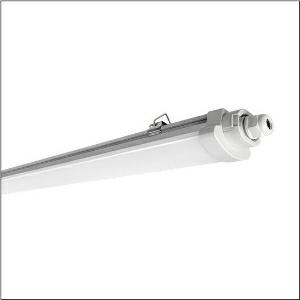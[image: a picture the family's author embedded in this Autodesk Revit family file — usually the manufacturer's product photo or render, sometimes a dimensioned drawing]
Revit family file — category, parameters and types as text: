
# Revit family: monsun_r__41_51fk20mn460a_a5b0
name_source: partatom
category: Lighting Fixtures
units: mm (PartAtom-declared; Revit-internal decimal feet)

## family parameters
Cut with Voids When Loaded = No
Host = Face
Light Source = No
Part Type = Normal
Room Calculation Point = No
Round Connector Dimension = Use Diameter
Shared = No

## types (1)
- --- (1 x LED, 6000 lm, 46 W, 4000K)
    Apparent Load = 46 VA
    CIE Flux Codes = 44 74 91 91 100
    Color Rendering = 80
    Color Temperature = 4000K
    Default Elevation = 1800 mm
    Description = Monsun® 41, damp-proof luminaire, primary optical cover: diffuser, of PC, frosted, light emission: direct distribution, primary light characteristic: symmetric, installation type: suspended mounting, surface-mounted, LED, rated luminous flux: 6.000lm, luminous efficacy: 130lm/W, light colour: 840, colour temperature: 4000K, control gear: ON/OFF Multilumen, with terminal, 3-pole, mains connection: 220..240V, AC, 50/60Hz, rated input power: 46W, housing, luminaire housing, of PC, grey, length: 1.500mm, width: 79mm, height: 52mm, end cap, of PC, grey, ceiling mounting element, of stainless steel (V2A), protection rating (complete): IP65, insulation class (complete): insulation class II (safety insulation), certification: CE, UKCA, protection symbol: D, impact resistance: IK08, permissible operating ambient temperature: -20..+35°C, corresponds to IFS (International Featured Standards) requirements for safety and quality in the food industry, contact your sales advisor before using the luminaires in applications with unclear chemical exposure, large temperature fluctuations or condensation-forming humidity, packaging unit: 1 piece
    Height = 54 mm
    Lamp = 1 x LED
    Lamp Light Flux = 6000 lm
    Lamp Power = 46 W
    Lamp count = 1
    Length = 1500 mm
    Luminous efficacy = 130 lm/W
    Manufacturer = Siteco
    ModVariant = No
    Model = 51FK20MN460A
    Mounting Place = Ceiling
    Mounting Type = Surface mounted
    Number of Poles = 1
    OnlyDefault = Yes
    Power Factor = 1
    Product Name = Monsun® 41
    Product group = damp-proof luminaire
    ProductGroupID = 301
    Protection Class = Protection class II
    Protection Degree = IP 65
    RLX_Detail_Level = 1
    RLX_Emergency_Light_Flux = 0 lm
    RLX_Emergency_Type = 0
    RLX_Emergency_Type_DB = No
    RlxData = <blob elided: 29001 chars, md5=018f6827>
    Socket = socket
    Standby Power = 0 W
    System Light Flux = 6000 lm
    System Power = 46 W
    Type Comments = factory setting: luminous flux: 100 % | (HIGH)
    Type Image = l_1007037.jpg
    URL = http://relux.com
    VarID = @adj_196167
    Voltage = 0 V
    Weight = 0.00 kg
    Width = 79 mm

## geometry (parser evidence)
native form markers: Blend x4, Sweep x11
no freeform markers — native parametric forms only
